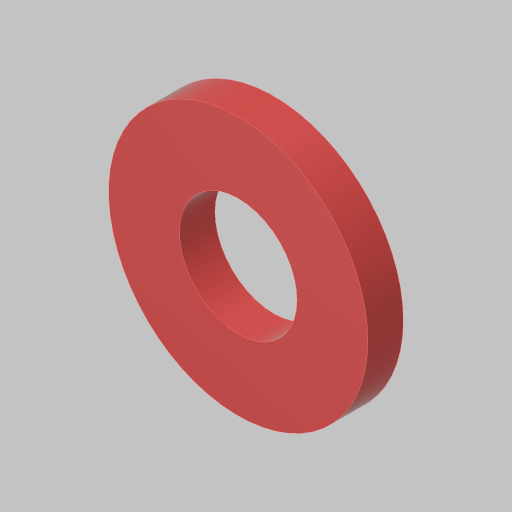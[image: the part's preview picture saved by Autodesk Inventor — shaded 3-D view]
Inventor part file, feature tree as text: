
AUTODESK INVENTOR PART (.ipt)
format: ipt  version: 2023.5 (Build 275446000, 446)  size: 101,376 bytes
history: native  units: in
note: dims shown in document units (in); Inventor stores cm internally (conversion verified against a paired STEP export)
features: extrude x1, sketch x1
ambient origin geometry x8: Origin, YZ Plane, XZ Plane, XY Plane, X Axis, Y Axis, Z Axis, Center Point
bodies: Solid1 (feature_tree)
feature tree (2):
  extrude  "Extrusion1"  Depth=0.125in
  sketch  "Sketch1"  dims[d0=0.25in d1=0.415in d2=0.125in d3=0.0in]
